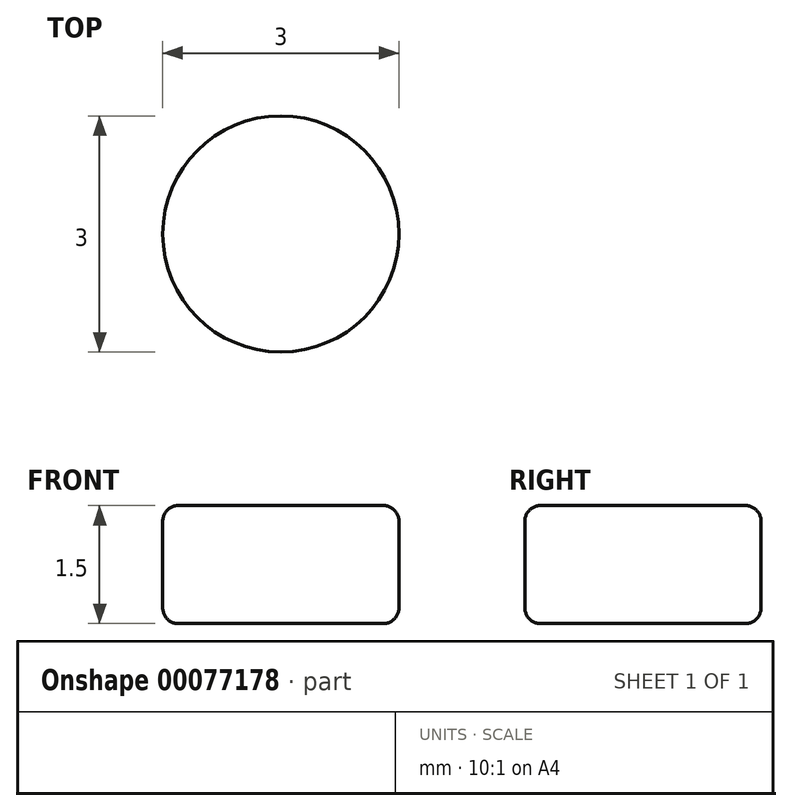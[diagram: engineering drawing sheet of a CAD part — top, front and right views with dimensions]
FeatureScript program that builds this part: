
annotation { "Feature Type Name" : "Feature", "Feature Type Description" : "" }
export const myFeature = defineFeature(function(context is Context, id is Id, definition is map)
    precondition{}
    {
        {
            var Q0;
            Q0=qCreatedBy(makeId("Top.planeOp"),FACE);
            var sketch = newSketch(context, id + "F0", { "sketchPlane" : qUnion([Q0])});
            skCircle(sketch, "E0", {"center": v(0, 0) * mm, "radius": 1.5 * mm});
            skSolve(sketch);
        }
        {
            var Q0;
            Q0=qSketchRegion(id+"F0",true);
            extrude(context, id + "F1", {"entities" : qUnion([Q0]), "depth" : 1.5 * mm});
        }
        {
            var Q0;
            Q0=makeQuery(id+"F1.opExtrude","CAP_EDGE",EDGE,{"disambiguationData":[OSD([sQuery(id+"F0.wireOp",EDGE,"E0")])],"isStart":false});
            var Q1;
            Q1=makeQuery(id+"F1.opExtrude","CAP_EDGE",EDGE,{"disambiguationData":[OSD([sQuery(id+"F0.wireOp",EDGE,"E0")])],"isStart":true});
            fillet(context, id + "F2", {"entities" : qUnion([Q0, Q1]), "radius" : .2 * mm, "tangentPropagation" : true, "allowEdgeOverflow" : false});
        }
    });
